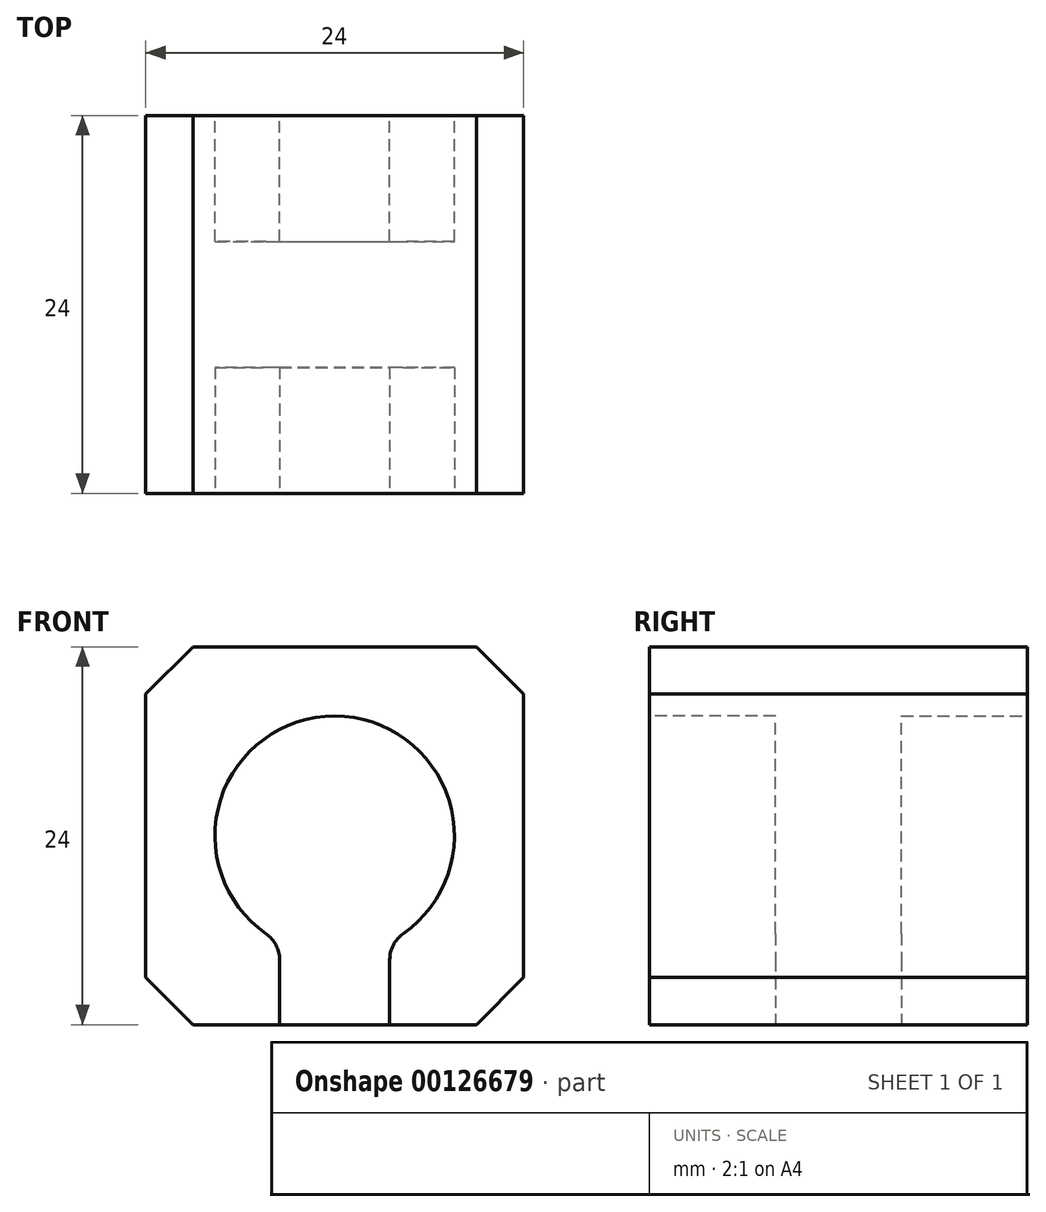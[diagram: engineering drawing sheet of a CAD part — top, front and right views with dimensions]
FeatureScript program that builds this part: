
annotation { "Feature Type Name" : "Feature", "Feature Type Description" : "" }
export const myFeature = defineFeature(function(context is Context, id is Id, definition is map)
    precondition{}
    {
        {
            var Q0;
            Q0=qCreatedBy(makeId("Front.planeOp"),FACE);
            var sketch = newSketch(context, id + "F0", { "sketchPlane" : qUnion([Q0])});
            skLineSegment(sketch, "E0.bottom", {"start": v(-12, 12) * mm, "end": v(12, 12) * mm});
            skLineSegment(sketch, "E0.top", {"start": v(-12, -12) * mm, "end": v(12, -12) * mm});
            skLineSegment(sketch, "E0.left", {"start": v(-12, 12) * mm, "end": v(-12, -12) * mm});
            skLineSegment(sketch, "E0.right", {"start": v(12, 12) * mm, "end": v(12, -12) * mm});
            skSolve(sketch);
        }
        {
            var Q0;
            Q0=makeQuery(id+"F0.imprint","IMPRINT",FACE,{"disambiguationData":[TD([[makeQuery(id+"F0.imprint","IMPRINT",EDGE,{"derivedFrom":sQuery(id+"F0.wireOp",EDGE,"E0.bottom")}),-1.0]])]});
            extrude(context, id + "F1", {"entities" : qUnion([Q0]), "endBound" : BoundingType.SYMMETRIC, "depth" : 24 * mm});
        }
        {
            var Q0;
            Q0=makeQuery(id+"F1.opExtrude","SWEPT_EDGE",EDGE,{"disambiguationData":[OSD([sQuery(id+"F0.wireOp",EDGE,"E0.bottom"),sQuery(id+"F0.wireOp",EDGE,"E0.right")])]});
            var Q1;
            Q1=makeQuery(id+"F1.opExtrude","SWEPT_EDGE",EDGE,{"disambiguationData":[OSD([sQuery(id+"F0.wireOp",EDGE,"E0.top"),sQuery(id+"F0.wireOp",EDGE,"E0.right")])]});
            var Q2;
            Q2=makeQuery(id+"F1.opExtrude","SWEPT_EDGE",EDGE,{"disambiguationData":[OSD([sQuery(id+"F0.wireOp",EDGE,"E0.top"),sQuery(id+"F0.wireOp",EDGE,"E0.left")])]});
            var Q3;
            Q3=makeQuery(id+"F1.opExtrude","SWEPT_EDGE",EDGE,{"disambiguationData":[OSD([sQuery(id+"F0.wireOp",EDGE,"E0.bottom"),sQuery(id+"F0.wireOp",EDGE,"E0.left")])]});
            chamfer(context, id + "F2", {"entities" : qUnion([Q0, Q1, Q2, Q3]), "width" : 3 * mm, "tangentPropagation" : true});
        }
        {
            var Q0;
            Q0=makeQuery(id+"F1.opExtrude","CAP_FACE",FACE,{"disambiguationData":[OSD([sQuery(id+"F0.wireOp",EDGE,"E0.bottom"),sQuery(id+"F0.wireOp",EDGE,"E0.top"),sQuery(id+"F0.wireOp",EDGE,"E0.left"),sQuery(id+"F0.wireOp",EDGE,"E0.right")])],"isStart":false});
            var sketch = newSketch(context, id + "F3", { "sketchPlane" : qUnion([Q0])});
            skCircle(sketch, "E1", {"center": v(0, 0) * mm, "radius": 7.6 * mm});
            skLineSegment(sketch, "E2.bottom", {"start": v(-3.5, -5.06) * mm, "end": v(3.5, -5.06) * mm});
            skLineSegment(sketch, "E2.top", {"start": v(-3.5, -12) * mm, "end": v(3.5, -12) * mm});
            skLineSegment(sketch, "E2.left", {"start": v(-3.5, -5.06) * mm, "end": v(-3.5, -12) * mm});
            skLineSegment(sketch, "E2.right", {"start": v(3.5, -5.06) * mm, "end": v(3.5, -12) * mm});
            skSolve(sketch);
        }
        {
            var Q0;
            Q0=makeQuery(id+"F1.opExtrude","CAP_FACE",FACE,{"disambiguationData":[OSD([sQuery(id+"F0.wireOp",EDGE,"E0.bottom"),sQuery(id+"F0.wireOp",EDGE,"E0.top"),sQuery(id+"F0.wireOp",EDGE,"E0.left"),sQuery(id+"F0.wireOp",EDGE,"E0.right")])],"isStart":true});
            var sketch = newSketch(context, id + "F4", { "sketchPlane" : qUnion([Q0])});
            skCircle(sketch, "E3", {"center": v(0, 0) * mm, "radius": 7.6 * mm});
            skLineSegment(sketch, "E4.bottom", {"start": v(-3.5, -5) * mm, "end": v(3.5, -5) * mm});
            skLineSegment(sketch, "E4.top", {"start": v(-3.5, -12) * mm, "end": v(3.5, -12) * mm});
            skLineSegment(sketch, "E4.left", {"start": v(-3.5, -5) * mm, "end": v(-3.5, -12) * mm});
            skLineSegment(sketch, "E4.right", {"start": v(3.5, -5) * mm, "end": v(3.5, -12) * mm});
            skSolve(sketch);
        }
        {
            var Q0;
            Q0 = qSketchRegion(id + "F3", true);
            extrude(context, id + "F5", {"entities" : qUnion([Q0]), "operationType" : NewBodyOperationType.REMOVE, "oppositeDirection" : true, "depth" : 8 * mm});
        }
        {
            var Q0;
            Q0 = qSketchRegion(id + "F4", true);
            extrude(context, id + "F6", {"entities" : qUnion([Q0]), "operationType" : NewBodyOperationType.REMOVE, "oppositeDirection" : true, "depth" : 8 * mm});
        }
        {
            var Q0;
            Q0=makeQuery(id+"F6.boolean.opBoolean","COPY",EDGE,{"derivedFrom":makeQuery(id+"F6.opExtrude","SWEPT_EDGE",EDGE,{"disambiguationData":[OSD([sQuery(id+"F4.wireOp",EDGE,"E3"),sQuery(id+"F4.wireOp",EDGE,"E4.left")])]})});
            var Q1;
            Q1=makeQuery(id+"F6.boolean.opBoolean","COPY",EDGE,{"derivedFrom":makeQuery(id+"F6.opExtrude","SWEPT_EDGE",EDGE,{"disambiguationData":[OSD([sQuery(id+"F4.wireOp",EDGE,"E3"),sQuery(id+"F4.wireOp",EDGE,"E4.right")])]})});
            var Q2;
            Q2=makeQuery(id+"F5.boolean.opBoolean","COPY",EDGE,{"derivedFrom":makeQuery(id+"F5.opExtrude","SWEPT_EDGE",EDGE,{"disambiguationData":[OSD([sQuery(id+"F3.wireOp",EDGE,"E1"),sQuery(id+"F3.wireOp",EDGE,"E2.right")])]})});
            var Q3;
            Q3=makeQuery(id+"F5.boolean.opBoolean","COPY",EDGE,{"derivedFrom":makeQuery(id+"F5.opExtrude","SWEPT_EDGE",EDGE,{"disambiguationData":[OSD([sQuery(id+"F3.wireOp",EDGE,"E1"),sQuery(id+"F3.wireOp",EDGE,"E2.left")])]})});
            fillet(context, id + "F7", {"entities" : qUnion([Q0, Q1, Q2, Q3]), "radius" : 2 * mm, "tangentPropagation" : true, "allowEdgeOverflow" : false});
        }
        {
            var Q0;
            Q0=makeQuery(id+"F1.opExtrude","SWEPT_BODY",BODY,{"disambiguationData":[OSD([sQuery(id+"F0.wireOp",EDGE,"E0.bottom"),sQuery(id+"F0.wireOp",EDGE,"E0.top"),sQuery(id+"F0.wireOp",EDGE,"E0.left"),sQuery(id+"F0.wireOp",EDGE,"E0.right")])]});
            transform(context, id + "F8", {"entities" : qUnion([Q0]), "transformType" : TransformType.TRANSLATION_3D, "dx" : 0 * mm, "dy" : 0 * mm, "dz" : 0 * mm, "makeCopy" : true});
        }
    });
